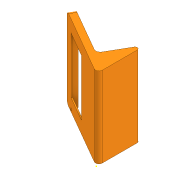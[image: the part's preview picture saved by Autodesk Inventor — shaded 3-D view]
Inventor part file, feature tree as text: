
AUTODESK INVENTOR PART (.ipt)
format: ipt  version: 2020.3 (Build 243373000, 373)  size: 200,192 bytes
history: native  units: mm
features: sketch x5, extrude x4, fillet x4, other x1
ambient origin geometry x8: Origin, YZ Plane, XZ Plane, XY Plane, X Axis, Y Axis, Z Axis, Center Point
bodies: Solid1 (feature_tree)
feature tree (14):
  extrude  "Extrusion1"  Depth=72.0mm
  extrude  "Extrusion2"  Depth=5.5mm
  extrude  "Extrusion3"  Depth=25.17mm
  fillet  "Fillet1"  Radius=50.25mm
  fillet  "Fillet2"  Radius=10.0mm
  fillet  "Fillet3"  Radius=7.0mm
  fillet  "Fillet4"  Radius=32.0mm
  extrude  "Extrusion4"  Depth=2.66mm
  sketch  "Sketch5"  dims[d14=4.5mm d15=0.0mm d16=3.0mm d17=2.0mm d18=4.0mm d19=90.0deg d20=4.0mm d21=3.1mm d22=16.41mm d23=3.5mm d24=3.1mm d25=31.0mm d26=3.2mm d27=38.0mm d28=3.2mm d29=38.0mm d30=4.5mm d31=0.0mm d66=2.0mm d67=8.72mm d68=0.2mm]
  sketch  "Sketch1"  dims[d0=72.0mm d1=50.0mm]
  sketch  "Sketch2"  dims[d2=60.0deg d3=5.5mm]
  sketch  "Sketch3"  dims[d4=72.0mm d5=0.0mm d6=25.17mm d7=50.25mm d8=10.0mm d9=7.0mm d10=0.0mm d11=32.0mm]
  sketch  "Sketch4"  dims[d12=65.0mm d13=2.66mm]
  other  "Image1"
